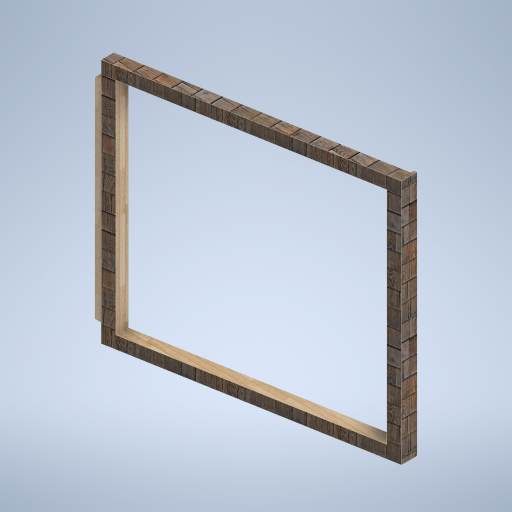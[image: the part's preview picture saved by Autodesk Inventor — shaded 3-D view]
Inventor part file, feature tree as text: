
AUTODESK INVENTOR PART (.ipt)
format: ipt  version: 2024.2 (Build 282272000, 272)  size: 377,344 bytes
history: native  units: in
note: dims shown in document units (in); Inventor stores cm internally (conversion verified against a paired STEP export)
features: sketch x9, plane x4, other x3
ambient origin geometry x8: Origin, YZ Plane, XZ Plane, XY Plane, X Axis, Y Axis, Z Axis, Center Point
bodies: Solid1 (feature_tree)
feature tree (16):
  other  "eave_frame_side_MIR.ipt"
  other  "Solid1::eave_frame_side_MIR.ipt"
  other  "TaggingFeature1"
  sketch  "Sketch1"  dims[d0=0.3937in]
  sketch  "Sketch2"
  sketch  "Sketch3"
  sketch  "Sketch4"
  sketch  "Sketch5"
  sketch  "Sketch6"
  sketch  "Sketch7"
  sketch  "Sketch8"
  sketch  "Sketch9"
  plane  "Work Plane1"
  plane  "Work Plane2"
  plane  "Work Plane3"
  plane  "Work Plane4"
